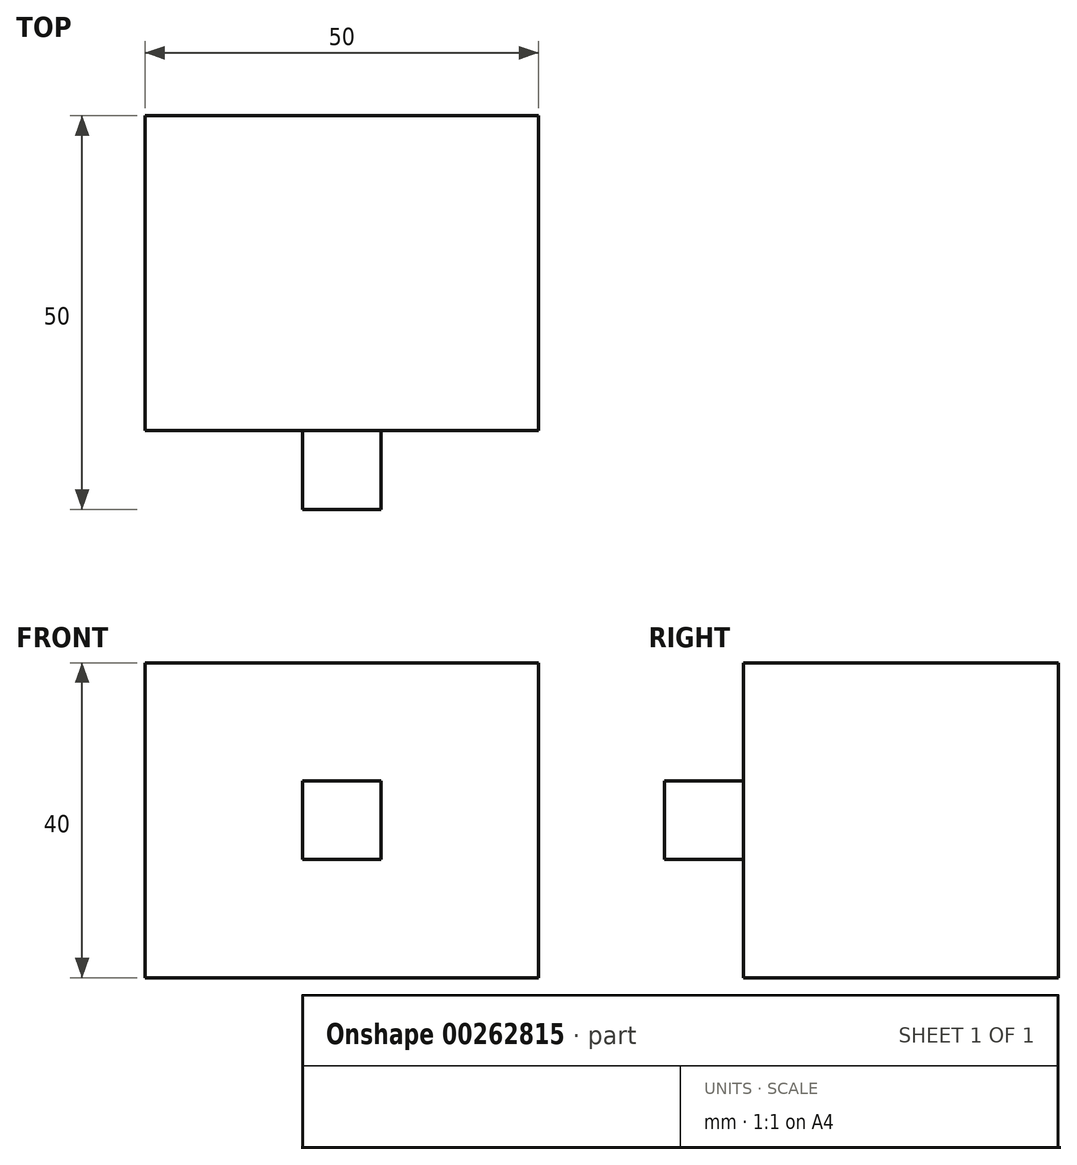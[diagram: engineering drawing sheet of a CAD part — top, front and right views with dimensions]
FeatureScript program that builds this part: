
annotation { "Feature Type Name" : "Feature", "Feature Type Description" : "" }
export const myFeature = defineFeature(function(context is Context, id is Id, definition is map)
    precondition{}
    {
        {
            var Q0;
            Q0=qCreatedBy(makeId("Front.planeOp"),FACE);
            var sketch = newSketch(context, id + "F0", { "sketchPlane" : qUnion([Q0])});
            skLineSegment(sketch, "E0.bottom", {"start": v(-25.87, 32.34) * mm, "end": v(24.13, 32.34) * mm});
            skLineSegment(sketch, "E0.top", {"start": v(-25.87, -7.66) * mm, "end": v(24.13, -7.66) * mm});
            skLineSegment(sketch, "E0.left", {"start": v(-25.87, 32.34) * mm, "end": v(-25.87, -7.66) * mm});
            skLineSegment(sketch, "E0.right", {"start": v(24.13, 32.34) * mm, "end": v(24.13, -7.66) * mm});
            skLineSegment(sketch, "E1.bottom", {"start": v(-5.87, 17.34) * mm, "end": v(4.13, 17.34) * mm});
            skLineSegment(sketch, "E1.top", {"start": v(-5.87, 7.34) * mm, "end": v(4.13, 7.34) * mm});
            skLineSegment(sketch, "E1.left", {"start": v(-5.87, 17.34) * mm, "end": v(-5.87, 7.34) * mm});
            skLineSegment(sketch, "E1.right", {"start": v(4.13, 17.34) * mm, "end": v(4.13, 7.34) * mm});
            skSolve(sketch);
        }
        {
            var Q0;
            Q0=makeQuery(id+"F0.imprint","IMPRINT",FACE,{"disambiguationData":[TD([[makeQuery(id+"F0.imprint","IMPRINT",EDGE,{"derivedFrom":sQuery(id+"F0.wireOp",EDGE,"E0.bottom")}),-1.0]])]});
            var Q1;
            Q1=makeQuery(id+"F0.imprint","IMPRINT",FACE,{"disambiguationData":[TD([[makeQuery(id+"F0.imprint","IMPRINT",EDGE,{"derivedFrom":sQuery(id+"F0.wireOp",EDGE,"E1.bottom")}),-1.0]])]});
            extrude(context, id + "F1", {"entities" : qUnion([Q0, Q1]), "oppositeDirection" : true, "depth" : 40 * mm});
        }
        {
            var Q0;
            Q0=makeQuery(id+"F1.opExtrude","CAP_FACE",FACE,{"disambiguationData":[OSD([sQuery(id+"F0.wireOp",EDGE,"E0.bottom"),sQuery(id+"F0.wireOp",EDGE,"E0.top"),sQuery(id+"F0.wireOp",EDGE,"E0.left"),sQuery(id+"F0.wireOp",EDGE,"E0.right")])],"isStart":false});
            var sketch = newSketch(context, id + "F2", { "sketchPlane" : qUnion([Q0])});
            skLineSegment(sketch, "E2.bottom", {"start": v(-24.13, -7.66) * mm, "end": v(25.87, -7.66) * mm});
            skLineSegment(sketch, "E2.top", {"start": v(-24.13, 12.34) * mm, "end": v(25.87, 12.34) * mm});
            skLineSegment(sketch, "E2.left", {"start": v(-24.13, -7.66) * mm, "end": v(-24.13, 12.34) * mm});
            skLineSegment(sketch, "E2.right", {"start": v(25.87, -7.66) * mm, "end": v(25.87, 12.34) * mm});
            skSolve(sketch);
        }
        {
            var Q0;
            Q0=makeQuery(id+"F1.opExtrude","SWEPT_FACE",FACE,{"disambiguationData":[OSD([sQuery(id+"F0.wireOp",EDGE,"E0.bottom")])]});
            var sketch = newSketch(context, id + "F3", { "sketchPlane" : qUnion([Q0])});
            skLineSegment(sketch, "E3.bottom", {"start": v(-25.87, 40) * mm, "end": v(24.13, 40) * mm});
            skLineSegment(sketch, "E3.top", {"start": v(-25.87, 30) * mm, "end": v(24.13, 30) * mm});
            skLineSegment(sketch, "E3.left", {"start": v(-25.87, 40) * mm, "end": v(-25.87, 30) * mm});
            skLineSegment(sketch, "E3.right", {"start": v(24.13, 40) * mm, "end": v(24.13, 30) * mm});
            skLineSegment(sketch, "E4.bottom", {"start": v(-25.87, 40) * mm, "end": v(-5.87, 40) * mm});
            skLineSegment(sketch, "E4.top", {"start": v(-25.87, 30) * mm, "end": v(-5.87, 30) * mm});
            skLineSegment(sketch, "E4.right", {"start": v(-5.87, 40) * mm, "end": v(-5.87, 30) * mm});
            skLineSegment(sketch, "E5.bottom", {"start": v(24.13, 30) * mm, "end": v(4.13, 30) * mm});
            skLineSegment(sketch, "E5.top", {"start": v(24.13, 40) * mm, "end": v(4.13, 40) * mm});
            skLineSegment(sketch, "E5.left", {"start": v(24.13, 30) * mm, "end": v(24.13, 40) * mm});
            skLineSegment(sketch, "E5.right", {"start": v(4.13, 30) * mm, "end": v(4.13, 40) * mm});
            skSolve(sketch);
        }
        {
            var Q0;
            Q0=makeQuery(id+"F0.imprint","IMPRINT",FACE,{"disambiguationData":[TD([[makeQuery(id+"F0.imprint","IMPRINT",EDGE,{"derivedFrom":sQuery(id+"F0.wireOp",EDGE,"E1.bottom")}),-1.0]])]});
            extrude(context, id + "F4", {"entities" : qUnion([Q0]), "operationType" : NewBodyOperationType.ADD, "depth" : 10 * mm});
        }
    });
